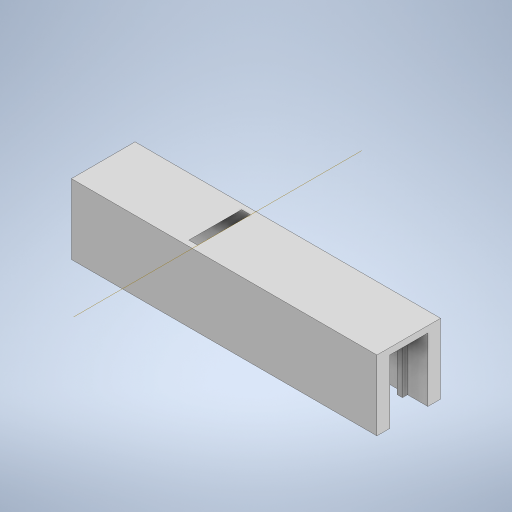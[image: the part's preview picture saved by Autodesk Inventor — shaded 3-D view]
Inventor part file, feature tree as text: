
AUTODESK INVENTOR PART (.ipt)
format: ipt  version: 2023 (Build 270158000, 158)  size: 444,928 bytes
history: native  units: in
note: dims shown in document units (in); Inventor stores cm internally (conversion verified against a paired STEP export)
features: extrude x8, sketch x8, plane x1
ambient origin geometry x8: Origin, YZ Plane, XZ Plane, XY Plane, X Axis, Y Axis, Z Axis, Center Point
bodies: Solid1 (feature_tree)
feature tree (17):
  extrude  "Extrusion1"  Depth=1.25in
  extrude  "Extrusion2"  Depth=0.55in
  extrude  "Extrusion3"  Depth=1.0in TaperAngle=0.0deg
  extrude  "Extrusion4"  TaperAngle=0.0deg  [1 undecoded]
  extrude  "Extrusion5"  Depth=0.0625in
  extrude  "Extrusion6"  Depth=0.25in
  plane  "Work Plane1"
  extrude  "Extrusion7"  Depth=0.1in
  extrude  "Extrusion8"  Depth=0.1in
  sketch  "Sketch1"  dims[d0=6.0in d1=1.25in]
  sketch  "Sketch2"  dims[d2=1.2in d3=0.55in]
  sketch  "Sketch3"  dims[d4=1.0in d5=0.07in d6=0.0in]
  sketch  "Sketch4"  dims[d7=1.2in d8=0.0in]
  sketch  "Sketch5"  dims[d9=0.07in d10=0.0in d11=0.0625in]
  sketch  "Sketch6"  dims[d12=0.25in d13=0.0in d14=0.25in]
  sketch  "Sketch7"  dims[d15=0.1in d16=0.1in]
  sketch  "Sketch8"  dims[d17=0.1in d18=0.1in d19=0.1in d20=0.1in d21=1.0in d22=0.1in d23=0.1in d24=0.1in d25=0.1in d26=0.1in d27=0.1in d28=0.1in d29=0.1in d30=0.1in d31=0.1in d32=0.1in d33=0.1in d34=1.0in d35=1.0in d36=1.0in d37=1.25in d38=0.0in d39=0.1in d40=0.1in d41=0.1in d42=0.1in d43=0.1in d44=0.1in d45=1.0in d46=1.0in d47=0.1in d48=0.1in d49=1.0in d50=0.1in d51=0.1in d52=1.0in d53=1.25in d54=0.0in d55=0.125in d56=0.0in d57=45.0deg d58=0.0in d59=5.0in d60=0.125in d61=0.0in d62=0.0in d63=0.0in]
note: 1 required parameter value undecoded (feature->parameter linkage not recoverable at this tier; creation-order binding heuristic only, values carry confidence <= 0.55)
